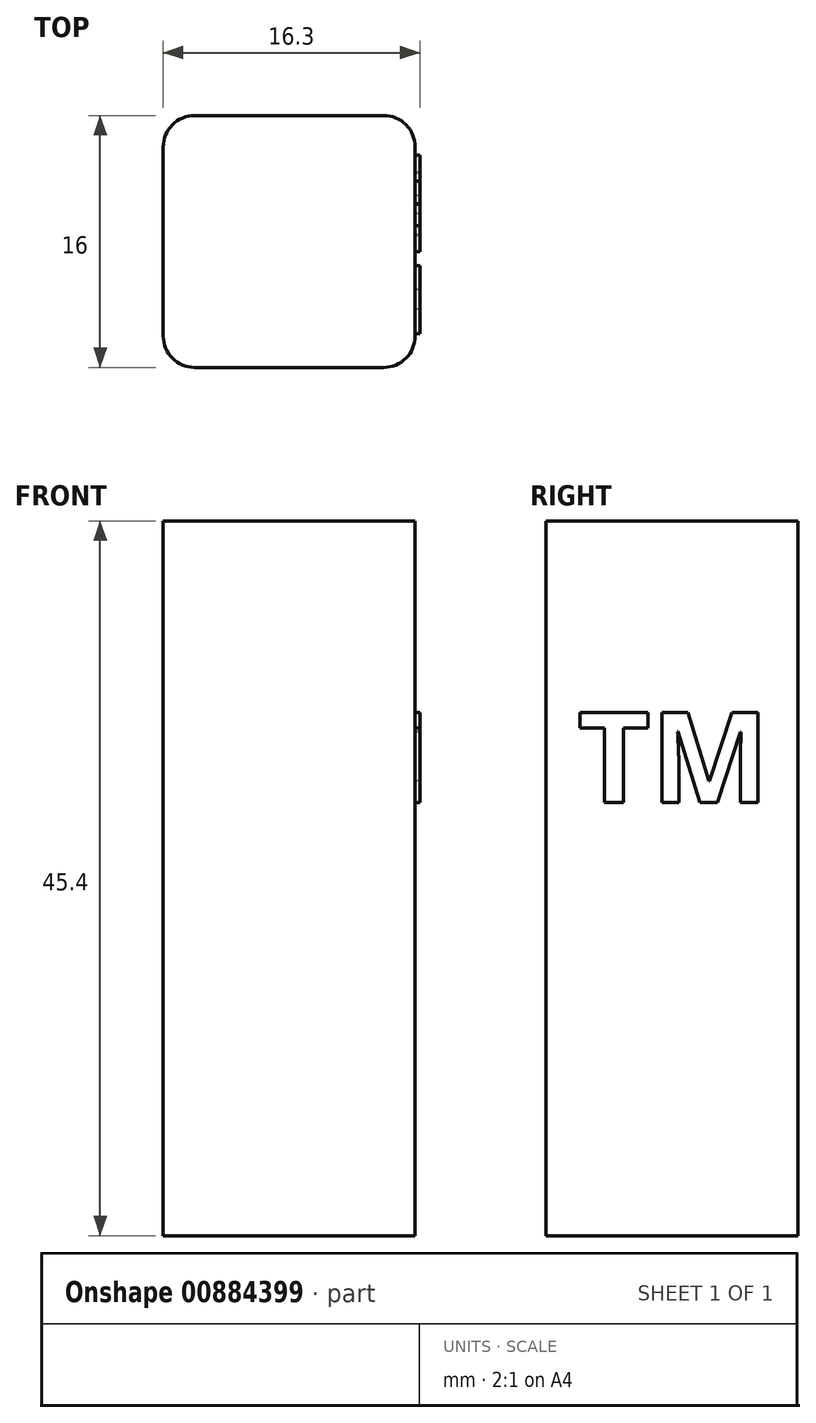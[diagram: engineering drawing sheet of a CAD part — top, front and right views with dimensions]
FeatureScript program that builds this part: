
annotation { "Feature Type Name" : "Feature", "Feature Type Description" : "" }
export const myFeature = defineFeature(function(context is Context, id is Id, definition is map)
    precondition{}
    {
        {
            var Q0;
            Q0=qCreatedBy(makeId("Top.planeOp"),FACE);
            var sketch = newSketch(context, id + "F0", { "sketchPlane" : qUnion([Q0])});
            skLineSegment(sketch, "E0.bottom", {"start": v(0, 0) * mm, "end": v(16, 0) * mm});
            skLineSegment(sketch, "E0.top", {"start": v(0, 16) * mm, "end": v(16, 16) * mm});
            skLineSegment(sketch, "E0.left", {"start": v(0, 0) * mm, "end": v(0, 16) * mm});
            skLineSegment(sketch, "E0.right", {"start": v(16, 0) * mm, "end": v(16, 16) * mm});
            skSolve(sketch);
        }
        {
            var Q0;
            Q0 = qSketchRegion(id + "F0", true);
            extrude(context, id + "F1", {"entities" : qUnion([Q0]), "depth" : 45.4 * mm, "offsetDistance" : 25 * mm});
        }
        {
            var Q0;
            Q0=makeQuery(id+"F1.opExtrude","SWEPT_EDGE",EDGE,{"disambiguationData":[OSD([sQuery(id+"F0.wireOp",EDGE,"E0.bottom"),sQuery(id+"F0.wireOp",EDGE,"E0.right")])]});
            var Q1;
            Q1=makeQuery(id+"F1.opExtrude","SWEPT_EDGE",EDGE,{"disambiguationData":[OSD([sQuery(id+"F0.wireOp",EDGE,"E0.bottom"),sQuery(id+"F0.wireOp",EDGE,"E0.left")])]});
            var Q2;
            Q2=makeQuery(id+"F1.opExtrude","SWEPT_EDGE",EDGE,{"disambiguationData":[OSD([sQuery(id+"F0.wireOp",EDGE,"E0.top"),sQuery(id+"F0.wireOp",EDGE,"E0.right")])]});
            var Q3;
            Q3=makeQuery(id+"F1.opExtrude","SWEPT_EDGE",EDGE,{"disambiguationData":[OSD([sQuery(id+"F0.wireOp",EDGE,"E0.top"),sQuery(id+"F0.wireOp",EDGE,"E0.left")])]});
            fillet(context, id + "F2", {"entities" : qUnion([Q0, Q1, Q2, Q3]), "radius" : 2 * mm, "tangentPropagation" : true, "allowEdgeOverflow" : false});
        }
        {
            var Q0;
            Q0=makeQuery(id+"F1.opExtrude","SWEPT_FACE",FACE,{"disambiguationData":[OSD([sQuery(id+"F0.wireOp",EDGE,"E0.right")])]});
            var sketch = newSketch(context, id + "F3", { "sketchPlane" : qUnion([Q0])});
            skText(sketch, "E1", { "text": "TM", "fontName": "OpenSans-Bold.ttf"});
            const initialGuessF3  = {"E1": [0.002, 0.02752, 1, 0, 0.00577]};
            skSetInitialGuess(sketch, initialGuessF3);
            skSolve(sketch);
        }
        {
            var Q0;
            Q0 = qSketchRegion(id + "F3", true);
            extrude(context, id + "F4", {"entities" : qUnion([Q0]), "operationType" : NewBodyOperationType.ADD, "depth" : 0.3 * mm, "offsetDistance" : 25 * mm});
        }
    });
